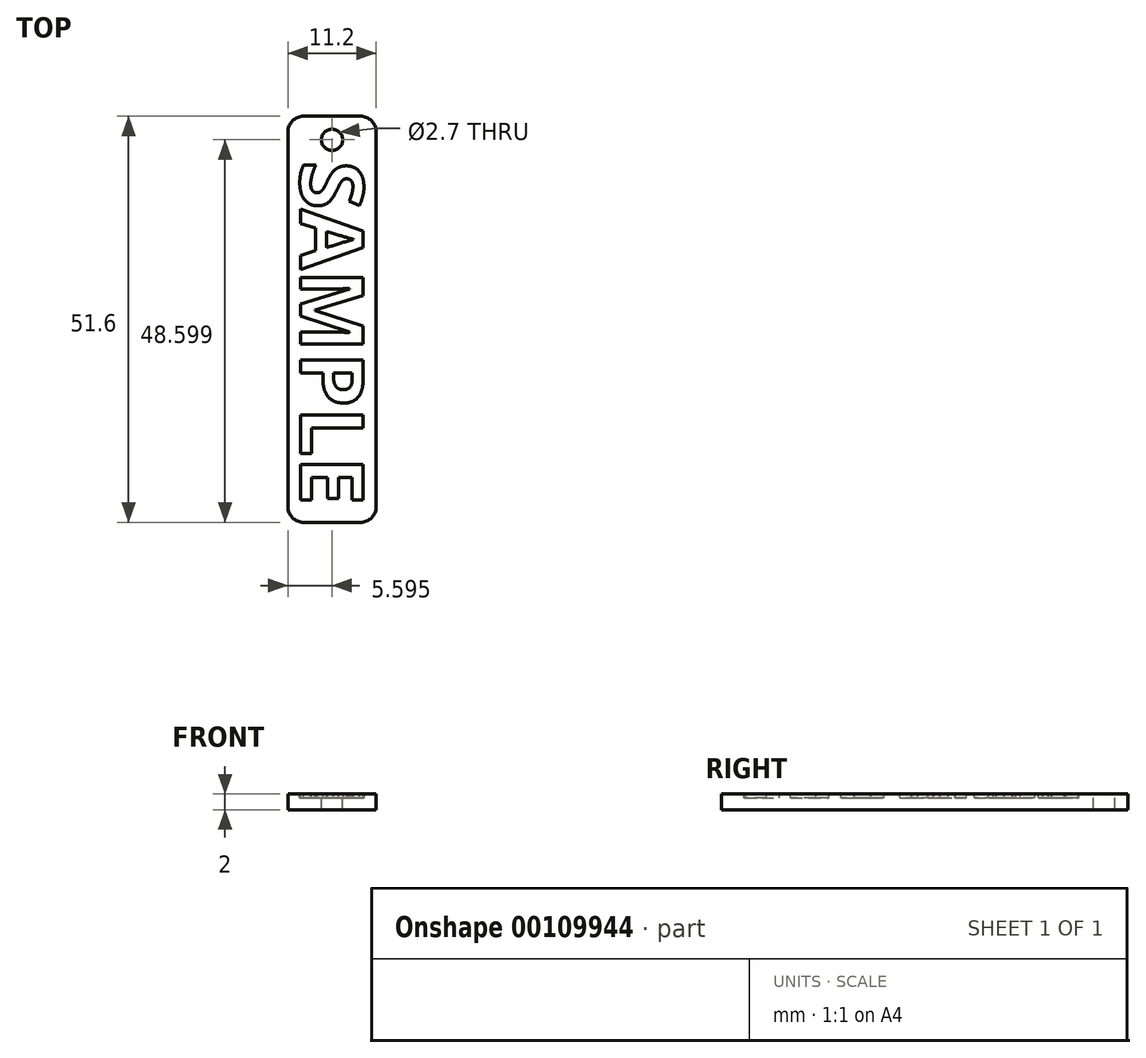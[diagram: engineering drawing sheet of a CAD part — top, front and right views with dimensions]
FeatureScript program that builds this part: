
annotation { "Feature Type Name" : "Feature", "Feature Type Description" : "" }
export const myFeature = defineFeature(function(context is Context, id is Id, definition is map)
    precondition{}
    {
        {
            var Q0;
            Q0=qCreatedBy(makeId("Top.planeOp"),FACE);
            var sketch = newSketch(context, id + "F0", { "sketchPlane" : qUnion([Q0])});
            skLineSegment(sketch, "E0.bottom", {"start": v(-49.86, 70.84) * mm, "end": v(-38.66, 70.84) * mm});
            skLineSegment(sketch, "E0.top", {"start": v(-49.86, 19.24) * mm, "end": v(-38.66, 19.24) * mm});
            skLineSegment(sketch, "E0.left", {"start": v(-49.86, 70.84) * mm, "end": v(-49.86, 19.24) * mm});
            skLineSegment(sketch, "E0.right", {"start": v(-38.66, 70.84) * mm, "end": v(-38.66, 19.24) * mm});
            skCircle(sketch, "E1", {"center": v(-44.26, 67.84) * mm, "radius": 1.35 * mm});
            skText(sketch, "E2", { "text": "SAMPLE", "fontName": "OpenSans-Bold.ttf"});
            const initialGuessF0  = {"E2": [-0.04826, 0.06514, 0, -1, 0.008]};
            skSetInitialGuess(sketch, initialGuessF0);
            skSolve(sketch);
        }
        {
            var Q0;
            Q0 = qSketchRegion(id + "F0", true);
            var Q1;
            Q1=makeQuery(id+"F0.imprint","IMPRINT",FACE,{"disambiguationData":[TD([[makeQuery(id+"F0.imprint","IMPRINT",EDGE,{"derivedFrom":sQuery(id+"F0.wireOp",EDGE,"E2.sketch_text.stroke-0")}),-1.0]])]});
            var Q2;
            Q2=makeQuery(id+"F0.imprint","IMPRINT",FACE,{"disambiguationData":[TD([[makeQuery(id+"F0.imprint","IMPRINT",EDGE,{"derivedFrom":sQuery(id+"F0.wireOp",EDGE,"E2.sketch_text.stroke-28")}),-1.0]])]});
            var Q3;
            Q3=makeQuery(id+"F0.imprint","IMPRINT",FACE,{"disambiguationData":[TD([[makeQuery(id+"F0.imprint","IMPRINT",EDGE,{"derivedFrom":sQuery(id+"F0.wireOp",EDGE,"E2.sketch_text.stroke-36")}),1.0]])]});
            var Q4;
            Q4=makeQuery(id+"F0.imprint","IMPRINT",FACE,{"disambiguationData":[TD([[makeQuery(id+"F0.imprint","IMPRINT",EDGE,{"derivedFrom":sQuery(id+"F0.wireOp",EDGE,"E2.sketch_text.stroke-40")}),-1.0]])]});
            var Q5;
            Q5=makeQuery(id+"F0.imprint","IMPRINT",FACE,{"disambiguationData":[TD([[makeQuery(id+"F0.imprint","IMPRINT",EDGE,{"derivedFrom":sQuery(id+"F0.wireOp",EDGE,"E2.sketch_text.stroke-59")}),-1.0]])]});
            var Q6;
            Q6=makeQuery(id+"F0.imprint","IMPRINT",FACE,{"disambiguationData":[TD([[makeQuery(id+"F0.imprint","IMPRINT",EDGE,{"derivedFrom":sQuery(id+"F0.wireOp",EDGE,"E2.sketch_text.stroke-59")}),1.0]])]});
            var Q7;
            Q7=makeQuery(id+"F0.imprint","IMPRINT",FACE,{"disambiguationData":[TD([[makeQuery(id+"F0.imprint","IMPRINT",EDGE,{"derivedFrom":sQuery(id+"F0.wireOp",EDGE,"E2.sketch_text.stroke-75")}),-1.0]])]});
            var Q8;
            Q8=makeQuery(id+"F0.imprint","IMPRINT",FACE,{"disambiguationData":[TD([[makeQuery(id+"F0.imprint","IMPRINT",EDGE,{"derivedFrom":sQuery(id+"F0.wireOp",EDGE,"E2.sketch_text.stroke-81")}),-1.0]])]});
            extrude(context, id + "F1", {"entities" : qUnion([Q0, Q1, Q2, Q3, Q4, Q5, Q6, Q7, Q8]), "oppositeDirection" : true, "depth" : 2 * mm});
        }
        {
            var Q0;
            Q0=makeQuery(id+"F0.imprint","IMPRINT",FACE,{"disambiguationData":[TD([[makeQuery(id+"F0.imprint","IMPRINT",EDGE,{"derivedFrom":sQuery(id+"F0.wireOp",EDGE,"E2.sketch_text.stroke-0")}),-1.0]])]});
            var Q1;
            Q1=makeQuery(id+"F0.imprint","IMPRINT",FACE,{"disambiguationData":[TD([[makeQuery(id+"F0.imprint","IMPRINT",EDGE,{"derivedFrom":sQuery(id+"F0.wireOp",EDGE,"E2.sketch_text.stroke-16")}),-1.0]])]});
            var Q2;
            Q2=makeQuery(id+"F0.imprint","IMPRINT",FACE,{"disambiguationData":[TD([[makeQuery(id+"F0.imprint","IMPRINT",EDGE,{"derivedFrom":sQuery(id+"F0.wireOp",EDGE,"E2.sketch_text.stroke-28")}),-1.0]])]});
            var Q3;
            Q3=makeQuery(id+"F0.imprint","IMPRINT",FACE,{"disambiguationData":[TD([[makeQuery(id+"F0.imprint","IMPRINT",EDGE,{"derivedFrom":sQuery(id+"F0.wireOp",EDGE,"E2.sketch_text.stroke-36")}),-1.0]])]});
            var Q4;
            Q4=makeQuery(id+"F0.imprint","IMPRINT",FACE,{"disambiguationData":[TD([[makeQuery(id+"F0.imprint","IMPRINT",EDGE,{"derivedFrom":sQuery(id+"F0.wireOp",EDGE,"E2.sketch_text.stroke-49")}),-1.0]])]});
            var Q5;
            Q5=makeQuery(id+"F0.imprint","IMPRINT",FACE,{"disambiguationData":[TD([[makeQuery(id+"F0.imprint","IMPRINT",EDGE,{"derivedFrom":sQuery(id+"F0.wireOp",EDGE,"E2.sketch_text.stroke-69")}),-1.0]])]});
            var Q6;
            Q6=makeQuery(id+"F0.imprint","IMPRINT",FACE,{"disambiguationData":[TD([[makeQuery(id+"F0.imprint","IMPRINT",EDGE,{"derivedFrom":sQuery(id+"F0.wireOp",EDGE,"E2.sketch_text.stroke-10")}),-1.0]])]});
            var Q7;
            Q7=makeQuery(id+"F0.imprint","IMPRINT",FACE,{"disambiguationData":[TD([[makeQuery(id+"F0.imprint","IMPRINT",EDGE,{"derivedFrom":sQuery(id+"F0.wireOp",EDGE,"E2.sketch_text.stroke-78")}),-1.0]])]});
            var Q8;
            Q8=makeQuery(id+"F0.imprint","IMPRINT",FACE,{"disambiguationData":[TD([[makeQuery(id+"F0.imprint","IMPRINT",EDGE,{"derivedFrom":sQuery(id+"F0.wireOp",EDGE,"E2.sketch_text.stroke-81")}),-1.0]])]});
            var Q9;
            Q9=qConstructionFilter(qBodyType(qCreatedBy(id+"F0",EDGE),BodyType.WIRE),ConstructionObject.NO);
            extrude(context, id + "F2", {"entities" : qUnion([Q0, Q1, Q2, Q3, Q4, Q5, Q6, Q7, Q8]), "operationType" : NewBodyOperationType.REMOVE, "surfaceEntities" : qUnion([Q9]), "oppositeDirection" : true, "depth" : .5 * mm});
        }
        {
            var Q0;
            Q0=makeQuery(id+"F1.opExtrude","SWEPT_EDGE",EDGE,{"disambiguationData":[OSD([sQuery(id+"F0.wireOp",EDGE,"E0.bottom"),sQuery(id+"F0.wireOp",EDGE,"E0.left")])]});
            var Q1;
            Q1=makeQuery(id+"F1.opExtrude","SWEPT_EDGE",EDGE,{"disambiguationData":[OSD([sQuery(id+"F0.wireOp",EDGE,"E0.bottom"),sQuery(id+"F0.wireOp",EDGE,"E0.right")])]});
            var Q2;
            Q2=makeQuery(id+"F1.opExtrude","SWEPT_EDGE",EDGE,{"disambiguationData":[OSD([sQuery(id+"F0.wireOp",EDGE,"E0.top"),sQuery(id+"F0.wireOp",EDGE,"E0.right")])]});
            var Q3;
            Q3=makeQuery(id+"F1.opExtrude","SWEPT_EDGE",EDGE,{"disambiguationData":[OSD([sQuery(id+"F0.wireOp",EDGE,"E0.top"),sQuery(id+"F0.wireOp",EDGE,"E0.left")])]});
            fillet(context, id + "F3", {"entities" : qUnion([Q0, Q1, Q2, Q3]), "radius" : 2 * mm, "tangentPropagation" : true, "allowEdgeOverflow" : false});
        }
    });
